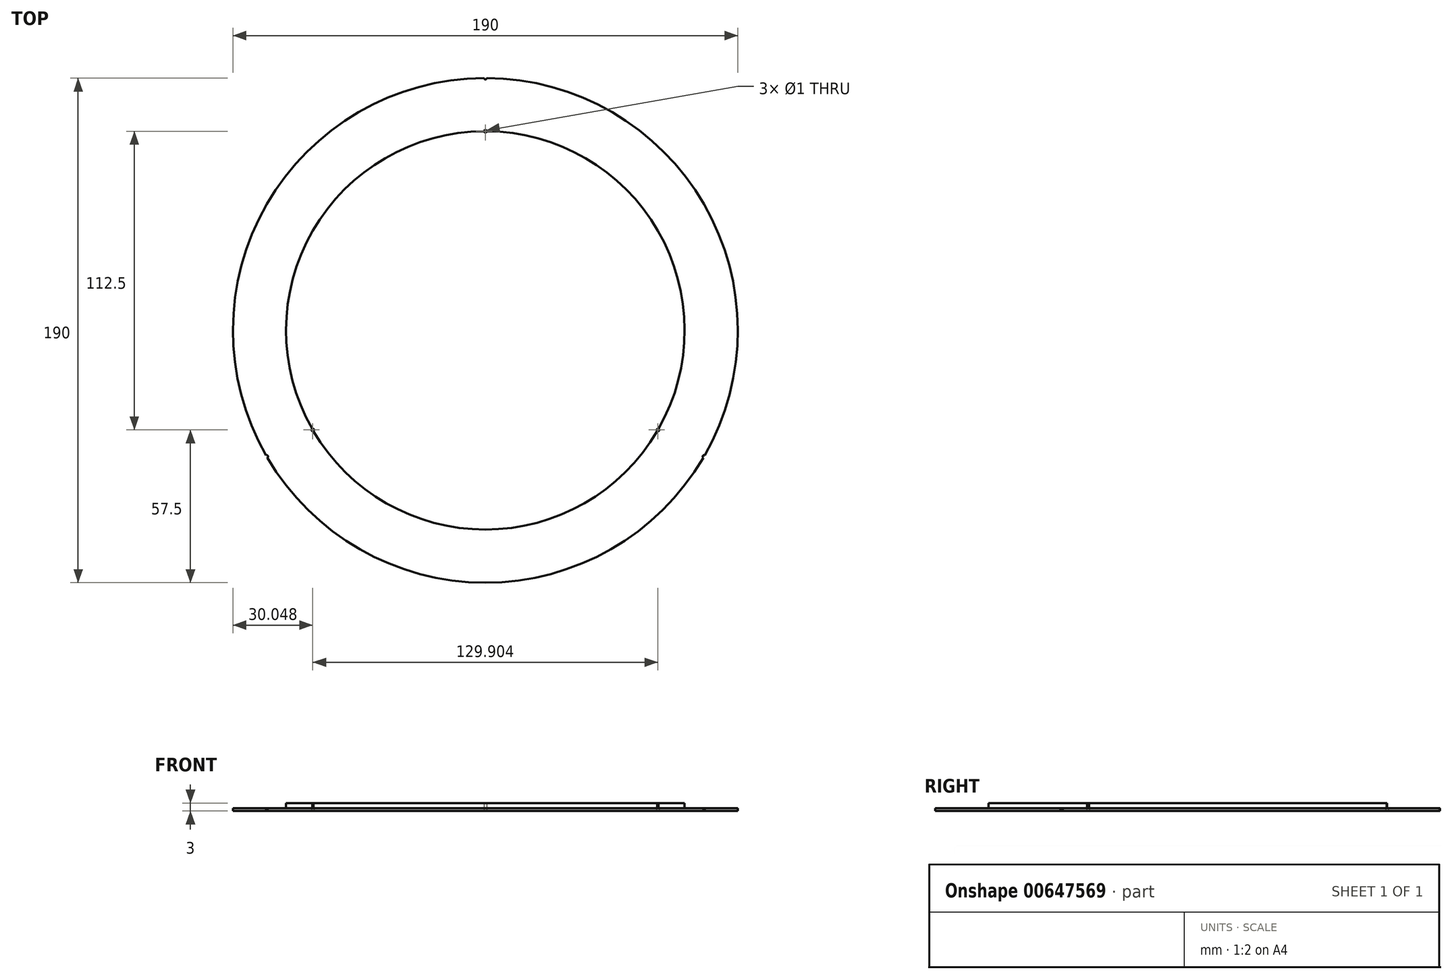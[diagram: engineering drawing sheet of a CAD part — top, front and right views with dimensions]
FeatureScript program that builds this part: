
annotation { "Feature Type Name" : "Feature", "Feature Type Description" : "" }
export const myFeature = defineFeature(function(context is Context, id is Id, definition is map)
    precondition{}
    {
        {
            var Q0;
            Q0=qCreatedBy(makeId("Top.planeOp"),FACE);
            var sketch = newSketch(context, id + "F0", { "sketchPlane" : qUnion([Q0])});
            skCircle(sketch, "E0", {"center": v(0, 0) * mm, "radius": 95 * mm});
            skLineSegment(sketch, "E1", {"start": v(0, 0) * mm, "end": v(0, 95) * mm, "construction": true});
            skLineSegment(sketch, "E2.1.0", {"start": v(0, 0) * mm, "end": v(-82.27, -47.5) * mm, "construction": true});
            skLineSegment(sketch, "E2.2.0", {"start": v(0, 0) * mm, "end": v(82.27, -47.5) * mm, "construction": true});
            skCircle(sketch, "E3", {"center": v(0, 0) * mm, "radius": 75 * mm});
            skPoint(sketch, "E4", {"position": v(0, 75) * mm});
            skPoint(sketch, "E5", {"position": v(-64.95, -37.5) * mm});
            skPoint(sketch, "E6", {"position": v(64.95, -37.5) * mm});
            skPoint(sketch, "E7", {"position": v(82.27, -47.5) * mm});
            skPoint(sketch, "E8", {"position": v(0, 95) * mm});
            skPoint(sketch, "E9", {"position": v(-82.27, -47.5) * mm});
            skSolve(sketch);
        }
        {
            var Q0;
            Q0=makeQuery(id+"F0.imprint","IMPRINT",FACE,{"disambiguationData":[TD([[makeQuery(id+"F0.imprint","IMPRINT",EDGE,{"derivedFrom":sQuery(id+"F0.wireOp",EDGE,"E0")}),1.0]])]});
            var Q1;
            Q1=makeQuery(id+"F0.imprint","IMPRINT",FACE,{"disambiguationData":[TD([[makeQuery(id+"F0.imprint","IMPRINT",EDGE,{"derivedFrom":sQuery(id+"F0.wireOp",EDGE,"E3")}),1.0]])]});
            extrude(context, id + "F1", {"entities" : qUnion([Q0, Q1]), "depth" : 1 * mm, "offsetDistance" : 25 * mm});
        }
        {
            var Q0;
            Q0=makeQuery(id+"F0.imprint","IMPRINT",FACE,{"disambiguationData":[TD([[makeQuery(id+"F0.imprint","IMPRINT",EDGE,{"derivedFrom":sQuery(id+"F0.wireOp",EDGE,"E3")}),1.0]])]});
            extrude(context, id + "F2", {"entities" : qUnion([Q0]), "operationType" : NewBodyOperationType.ADD, "depth" : 3 * mm, "offsetDistance" : 25 * mm});
        }
        {
            var Q0;
            Q0=sQuery(id+"F0.wireOp",VERTEX,"E4");
            var Q1;
            Q1=sQuery(id+"F0.wireOp",VERTEX,"E5");
            var Q2;
            Q2=sQuery(id+"F0.wireOp",VERTEX,"E6");
            var Q3;
            Q3=sQuery(id+"F0.wireOp",VERTEX,"E7");
            var Q4;
            Q4=sQuery(id+"F0.wireOp",VERTEX,"E9");
            var Q5;
            Q5=sQuery(id+"F0.wireOp",VERTEX,"E8");
            var Q6;
            Q6=makeQuery(id+"F1.opExtrude","SWEPT_BODY",BODY,{"disambiguationData":[OSD([sQuery(id+"F0.wireOp",EDGE,"E0")])]});
            hole(context, id + "F3", {"style" : HoleStyle.SIMPLE, "endStyle" : HoleEndStyle.THROUGH, "oppositeDirection" : true, "holeDiameter" : 1 * mm, "majorDiameter" : 5 * mm, "isTappedThrough" : true, "tappedDepth" : 12 * mm, "tapClearance" : 3, "startFromSketch" : true, "locations" : qUnion([Q0, Q1, Q2, Q3, Q4, Q5]), "scope" : qUnion([Q6])});
        }
    });
